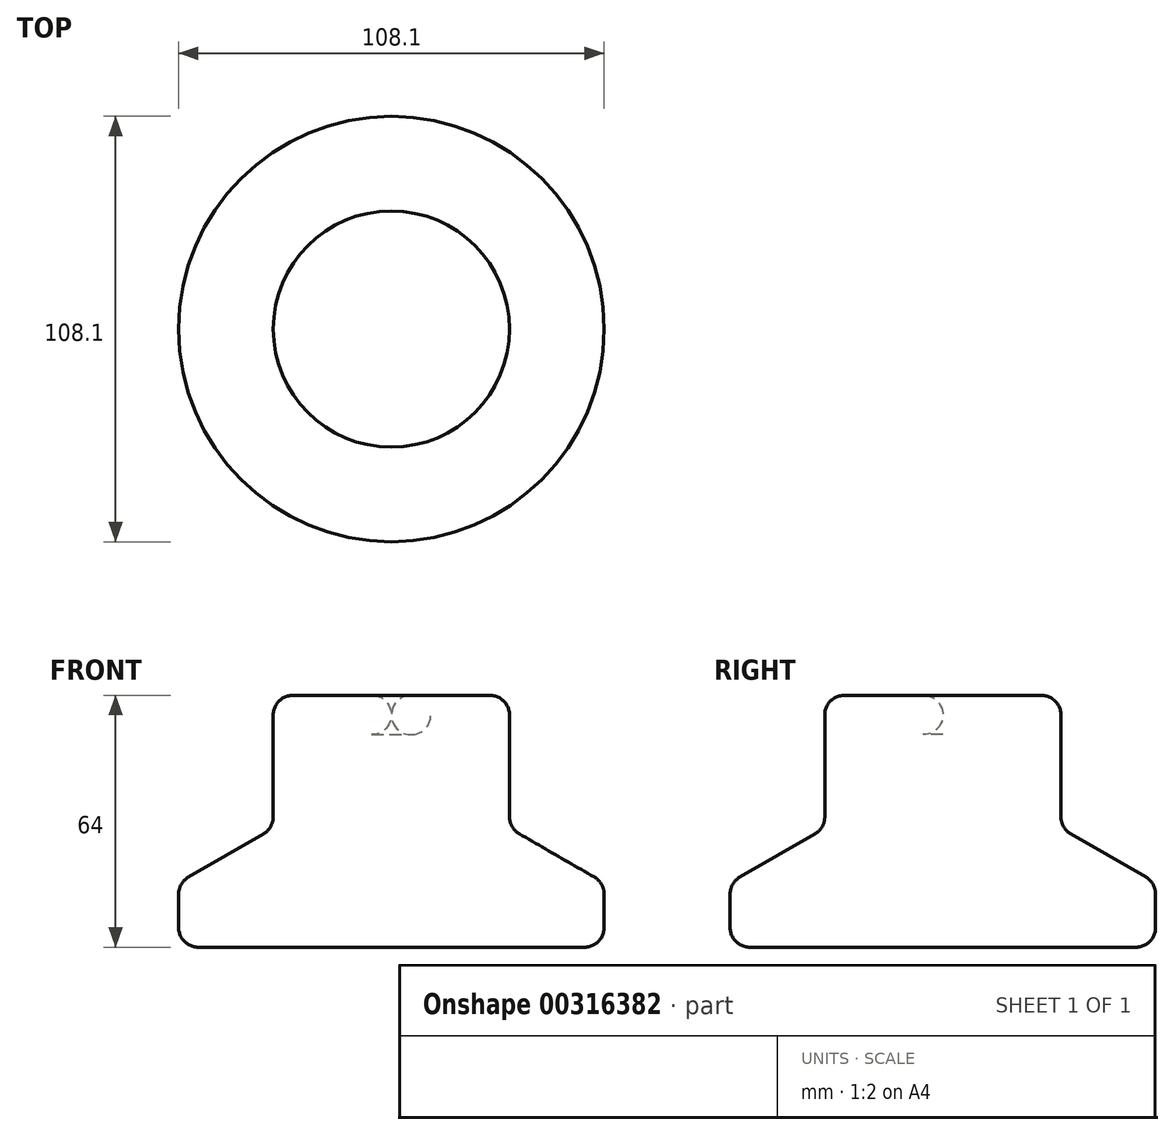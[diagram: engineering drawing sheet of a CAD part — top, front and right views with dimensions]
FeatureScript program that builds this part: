
annotation { "Feature Type Name" : "Feature", "Feature Type Description" : "" }
export const myFeature = defineFeature(function(context is Context, id is Id, definition is map)
    precondition{}
    {
        {
            var Q0;
            Q0=qCreatedBy(makeId("Front.planeOp"),FACE);
            var sketch = newSketch(context, id + "F0", { "sketchPlane" : qUnion([Q0])});
            skLineSegment(sketch, "E0", {"start": v(0, 5) * mm, "end": v(0, 59) * mm});
            skLineSegment(sketch, "E1", {"start": v(5, 64) * mm, "end": v(25, 64) * mm});
            skLineSegment(sketch, "E2", {"start": v(30, 59) * mm, "end": v(30, 33.13) * mm});
            skLineSegment(sketch, "E3", {"start": v(32.5, 28.8) * mm, "end": v(51.55, 17.8) * mm});
            skLineSegment(sketch, "E4", {"start": v(54.05, 13.47) * mm, "end": v(54.05, 5) * mm});
            skLineSegment(sketch, "E5", {"start": v(49.05, 0) * mm, "end": v(5, 0) * mm});
            skPoint(sketch, "E6.visualSharp", {"position": v(30, 30.24) * mm});
            skArc(sketch, "E6.filletArc", {"start": v(30, 33.13) * mm, "mid": v(30.67, 30.63) * mm, "end": v(32.5, 28.8) * mm});
            skPoint(sketch, "E7.visualSharp", {"position": v(54.05, 16.36) * mm});
            skArc(sketch, "E7.filletArc", {"start": v(54.05, 13.47) * mm, "mid": v(53.38, 15.97) * mm, "end": v(51.55, 17.8) * mm});
            skPoint(sketch, "E8.visualSharp", {"position": v(54.05, 0) * mm});
            skArc(sketch, "E8.filletArc", {"start": v(49.05, 0) * mm, "mid": v(52.59, 1.46) * mm, "end": v(54.05, 5) * mm});
            skPoint(sketch, "E9.visualSharp", {"position": v(30, 64) * mm});
            skArc(sketch, "E9.filletArc", {"start": v(30, 59) * mm, "mid": v(28.54, 62.54) * mm, "end": v(25, 64) * mm});
            skPoint(sketch, "E10.visualSharp", {"position": v(0, 64) * mm});
            skArc(sketch, "E10.filletArc", {"start": v(5, 64) * mm, "mid": v(1.46, 62.54) * mm, "end": v(0, 59) * mm});
            skPoint(sketch, "E11.visualSharp", {"position": v(0, 0) * mm});
            skArc(sketch, "E11.filletArc", {"start": v(0, 5) * mm, "mid": v(1.46, 1.46) * mm, "end": v(5, 0) * mm});
            skLineSegment(sketch, "E12", {"start": v(0, 74.73) * mm, "end": v(0, -71) * mm, "construction": true});
            skSolve(sketch);
        }
        {
            var Q0;
            Q0=makeQuery(id+"F0.imprint","IMPRINT",FACE,{"disambiguationData":[TD([[makeQuery(id+"F0.imprint","IMPRINT",EDGE,{"derivedFrom":sQuery(id+"F0.wireOp",EDGE,"E0")}),-1.0]])]});
            var Q1;
            Q1=sQuery(id+"F0.wireOp",EDGE,"E12");
            revolve(context, id + "F1", {"entities" : qUnion([Q0]), "axis" : qUnion([Q1]), "revolveType" : RevolveType.FULL});
        }
    });
